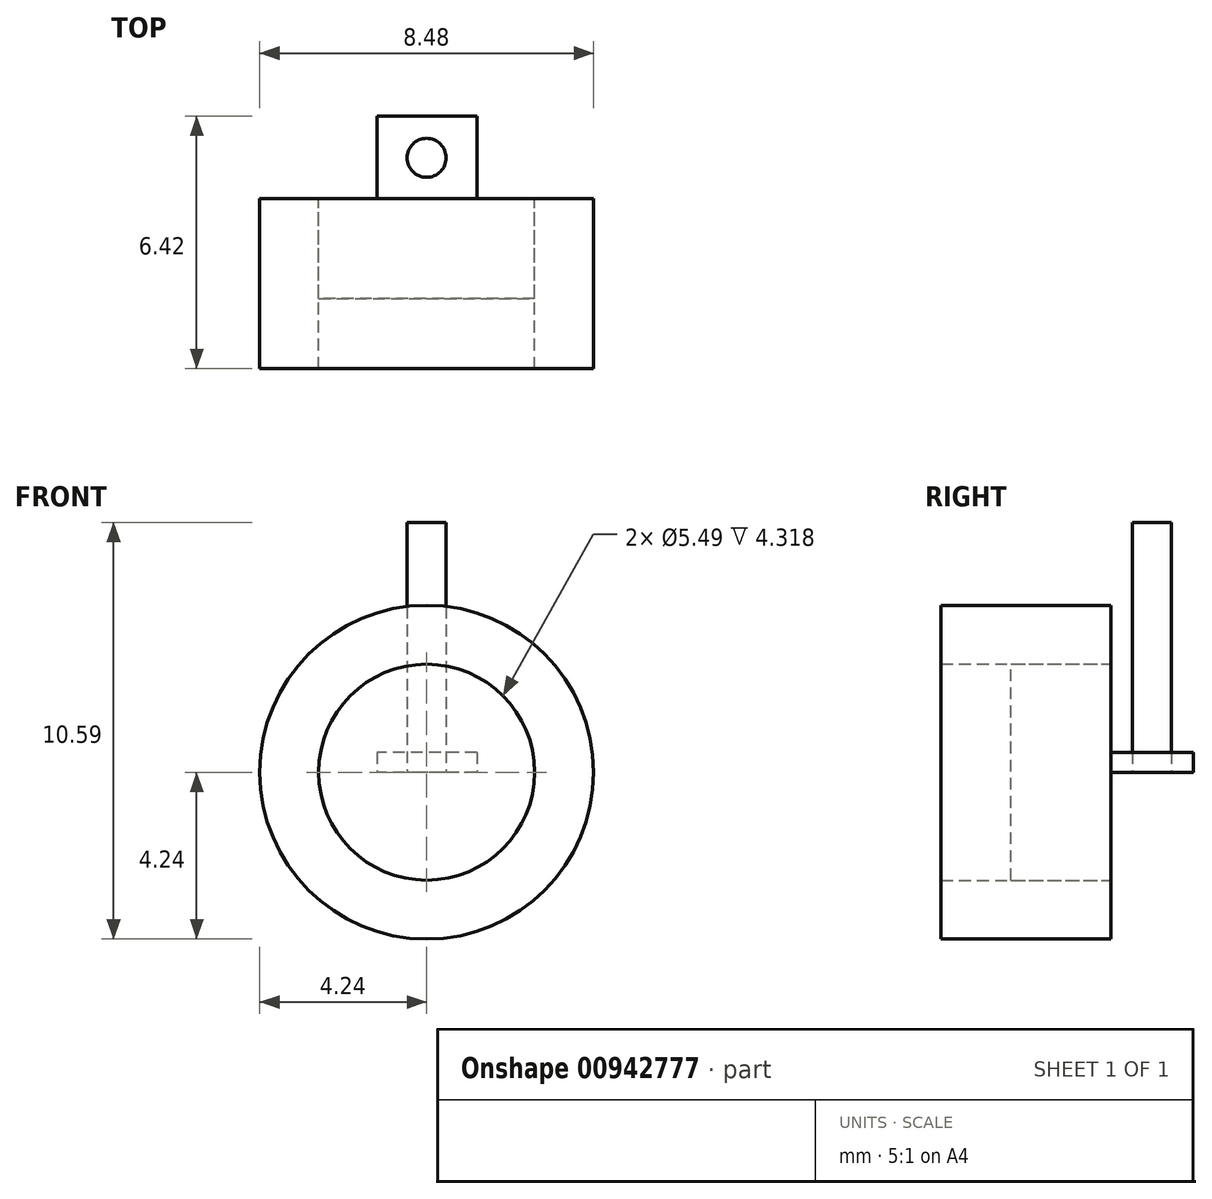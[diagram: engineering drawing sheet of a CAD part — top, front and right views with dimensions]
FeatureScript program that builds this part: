
annotation { "Feature Type Name" : "Feature", "Feature Type Description" : "" }
export const myFeature = defineFeature(function(context is Context, id is Id, definition is map)
    precondition{}
    {
        {
            var Q0;
            Q0=qCreatedBy(makeId("Front.planeOp"),FACE);
            var sketch = newSketch(context, id + "F0", { "sketchPlane" : qUnion([Q0])});
            skCircle(sketch, "E0", {"center": v(0, 0) * mm, "radius": 4.24 * mm});
            skCircle(sketch, "E1", {"center": v(0, 0) * mm, "radius": 2.74 * mm});
            skSolve(sketch);
        }
        {
            var Q0;
            Q0=qCreatedBy(makeId("Top.planeOp"),FACE);
            var sketch = newSketch(context, id + "F1", { "sketchPlane" : qUnion([Q0])});
            skCircle(sketch, "E2", {"center": v(0, 1.04) * mm, "radius": 0.5 * mm});
            skLineSegment(sketch, "E3", {"start": v(0, 0) * mm, "end": v(-1.27, 0) * mm});
            skLineSegment(sketch, "E4.bottom", {"start": v(-1.27, 0) * mm, "end": v(1.28, 0) * mm});
            skLineSegment(sketch, "E4.top", {"start": v(-1.27, 2.1) * mm, "end": v(1.28, 2.1) * mm});
            skLineSegment(sketch, "E4.left", {"start": v(-1.27, 0) * mm, "end": v(-1.27, 2.1) * mm});
            skLineSegment(sketch, "E4.right", {"start": v(1.28, 0) * mm, "end": v(1.28, 2.1) * mm});
            skSolve(sketch);
        }
        {
            var Q0;
            Q0=makeQuery(id+"F1.imprint","IMPRINT",FACE,{"disambiguationData":[TD([[makeQuery(id+"F1.imprint","IMPRINT",EDGE,{"derivedFrom":sQuery(id+"F1.wireOp",EDGE,"E2")}),-1.0]])]});
            var Q1;
            Q1=makeQuery(id+"F1.imprint","IMPRINT",FACE,{"disambiguationData":[TD([[makeQuery(id+"F1.imprint","IMPRINT",EDGE,{"derivedFrom":sQuery(id+"F1.wireOp",EDGE,"E2")}),1.0]])]});
            extrude(context, id + "F2", {"entities" : qUnion([Q0, Q1]), "depth" : 0.5 * mm, "offsetDistance" : 25.4 * mm});
        }
        {
            var Q0;
            Q0=makeQuery(id+"F1.imprint","IMPRINT",FACE,{"disambiguationData":[TD([[makeQuery(id+"F1.imprint","IMPRINT",EDGE,{"derivedFrom":sQuery(id+"F1.wireOp",EDGE,"E2")}),1.0]])]});
            extrude(context, id + "F3", {"entities" : qUnion([Q0]), "depth" : 6.35 * mm, "offsetDistance" : 25.4 * mm});
        }
        {
            var Q0;
            Q0=makeQuery(id+"F0.imprint","IMPRINT",FACE,{"disambiguationData":[TD([[makeQuery(id+"F0.imprint","IMPRINT",EDGE,{"derivedFrom":sQuery(id+"F0.wireOp",EDGE,"E0")}),1.0]])]});
            extrude(context, id + "F4", {"entities" : qUnion([Q0]), "depth" : 4.32 * mm, "offsetDistance" : 25.4 * mm});
        }
        {
            var Q0;
            Q0=makeQuery(id+"F0.imprint","IMPRINT",FACE,{"disambiguationData":[TD([[makeQuery(id+"F0.imprint","IMPRINT",EDGE,{"derivedFrom":sQuery(id+"F0.wireOp",EDGE,"E1")}),1.0]])]});
            extrude(context, id + "F5", {"entities" : qUnion([Q0]), "depth" : 2.54 * mm, "offsetDistance" : 25.4 * mm});
        }
    });
